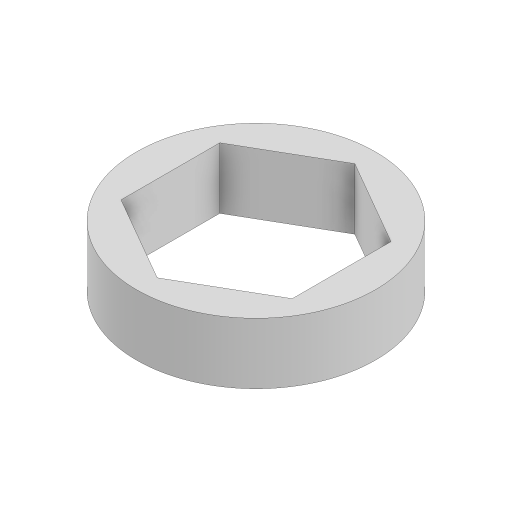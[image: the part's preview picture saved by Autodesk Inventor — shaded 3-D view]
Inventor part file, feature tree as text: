
AUTODESK INVENTOR PART (.ipt)
format: ipt  version: 2024 (Build 280153000, 153)  size: 102,912 bytes
history: native  units: mm
features: extrude x1, sketch x1
ambient origin geometry x8: Origin, YZ Plane, XZ Plane, XY Plane, X Axis, Y Axis, Z Axis, Center Point
bodies: Solid1 (feature_tree)
feature tree (2):
  extrude  "Extrusion1"  Depth=4.6mm
  sketch  "Sketch1"  dims[d0=12.9mm d1=18.0mm d2=4.6mm d3=0.0mm]
